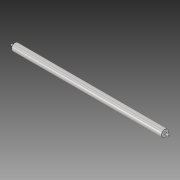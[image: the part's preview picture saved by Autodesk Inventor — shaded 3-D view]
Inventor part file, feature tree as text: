
AUTODESK INVENTOR PART (.ipt)
format: ipt  version: 2018 (Build 220112000, 112)  size: 87,040 bytes
history: native  units: in
note: dims shown in document units (in); Inventor stores cm internally (conversion verified against a paired STEP export)
features: revolve x1
ambient origin geometry x8: Origin, YZ Plane, XZ Plane, XY Plane, X Axis, Y Axis, Z Axis, Center Point
bodies: Solid1 (feature_tree)
feature tree (1):
  revolve  "Revolve1"  [1 undecoded]
note: 1 required parameter value undecoded (feature->parameter linkage not recoverable at this tier; creation-order binding heuristic only, values carry confidence <= 0.55)
